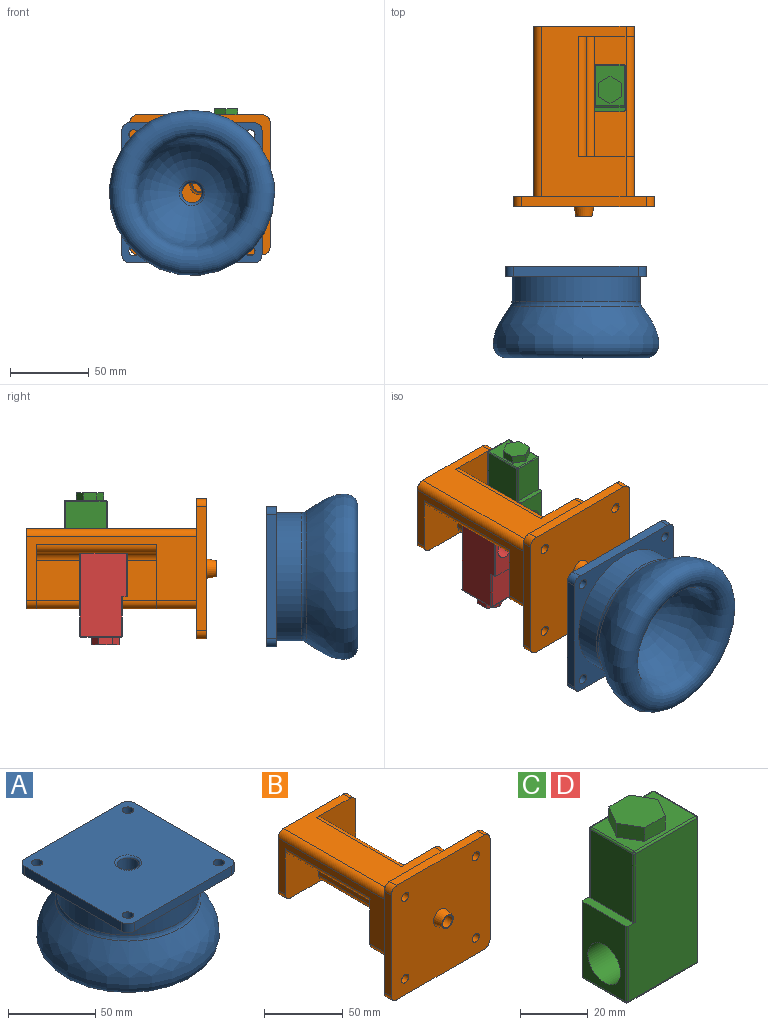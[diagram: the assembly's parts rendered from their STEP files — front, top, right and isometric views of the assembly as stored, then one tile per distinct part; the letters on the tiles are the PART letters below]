
ASSEMBLY  parts=4 mates=5
PART A: 20 faces, bbox 105x105x57.9 mm
  f0: plane 88.9x88.9mm, normal (0,0,-1), area 2565.7mm2, adj f1,f6,f7,f8,f9,f10,f11,f12
  f1: cylinder r=5.08mm len=6.35mm, axis (0,0,-1), area 50.7mm2, adj f0,f2,f6,f12
  f2: plane 88.9x88.9mm, normal (0,0,1), area 7572mm2, adj f1,f3,f6,f7,f8,f9,f10,f11
  f3: torus R=7.62mm, axis (0,0,1), area 85.4mm2, adj f2,f4
  f4: cylinder r=6.35mm len=15.18mm, axis (0,0,1), area 605.8mm2, adj f3,f5
  f5: torus R=9.53mm, axis (0,0,-1), area 151.2mm2, adj f4
  f6: plane 78.74x6.35mm, normal (-1,0,0), area 500mm2, adj f0,f1,f2,f7
  f7: cylinder r=5.08mm len=6.35mm, axis (0,0,1), area 50.7mm2, adj f0,f2,f6,f8
  f8: plane 78.74x6.35mm, normal (0,-1,0), area 500mm2, adj f0,f2,f7,f9
  f9: cylinder r=5.08mm len=6.35mm, axis (0,0,-1), area 50.7mm2, adj f0,f2,f8,f10
  f10: plane 78.74x6.35mm, normal (1,0,0), area 500mm2, adj f0,f2,f9,f11
  f11: cylinder r=5.08mm len=6.35mm, axis (0,0,1), area 50.7mm2, adj f0,f2,f10,f12
  f12: plane 78.74x6.35mm, normal (0,1,0), area 500mm2, adj f0,f1,f2,f11
  f13: cylinder r=3.17mm len=6.35mm, axis (0,0,1), area 126.7mm2, adj f0,f2
  f14: cylinder r=3.17mm len=6.35mm, axis (0,0,1), area 126.7mm2, adj f0,f2
  f15: cylinder r=3.17mm len=6.35mm, axis (0,0,1), area 126.7mm2, adj f0,f2
  f16: cylinder r=3.17mm len=6.35mm, axis (0,0,1), area 126.7mm2, adj f0,f2
  f17: cylinder r=40.64mm len=81.28mm, axis (0,0,1), area 4062mm2, adj f0,f18
  f18: torus R=45.72mm, axis (0,0,1), area 899mm2, adj f17
  f19: revolved ~104.97x104.97mm, area 44213.3mm2
PART B: 50 faces, bbox 88.9x120.7x88.9 mm
  f0: plane 53.34x20.32mm, normal (0,-1,0), area 830.5mm2, adj f14,f15,f16,f17,f18,f19
  f1: plane 40.64x35.24mm, normal (0,-1,0), area 1072.6mm2, adj f2,f3,f10,f11,f42,f43,f44,f46
  f2: plane 107.95x40.64mm, normal (1,0,0), area 1677.4mm2, adj f1,f7,f13,f31,f39,f42,f46,f47
  f3: plane 107.95x53.34mm, normal (0,0,1), area 3459.7mm2, adj f1,f7,f13,f31,f39,f44,f46,f49
  f4: plane 107.95x40.64mm, normal (-1,0,0), area 1677.4mm2, adj f6,f7,f12,f31,f38,f40,f48,f49
  f5: plane 107.95x53.34mm, normal (0,0,-1), area 3459.7mm2, adj f6,f7,f12,f31,f38,f45,f47,f48
  f6: plane 40.64x35.24mm, normal (0,-1,0), area 1072.6mm2, adj f4,f5,f8,f9,f40,f41,f45,f48
  f7: plane 63.5x50.8mm, normal (0,1,0), area 3203.6mm2, adj f2,f3,f4,f5,f46,f47,f48,f49
  f8: plane 76.2x20mm, normal (0,0,-1), area 1524.2mm2, adj f6,f12,f40,f41
  f9: plane 76.2x25.4mm, normal (-1,0,0), area 1935.5mm2, adj f6,f12,f41,f45
  f10: plane 76.2x20mm, normal (0,0,1), area 1524.2mm2, adj f1,f13,f42,f43
  f11: plane 76.2x25.4mm, normal (1,0,0), area 1935.5mm2, adj f1,f13,f43,f44
  f12: plane 40.64x35.24mm, normal (0,1,0), area 945.9mm2, adj f4,f5,f8,f9,f15,f38,f40,f41
  f13: plane 40.64x35.24mm, normal (0,1,0), area 945.9mm2, adj f2,f3,f10,f11,f14,f39,f42,f43
  f14: cylinder r=6.35mm len=12.7mm, axis (0,1,0), area 506.7mm2, adj f0,f13
  f15: cylinder r=6.35mm len=12.7mm, axis (0,1,0), area 506.7mm2, adj f0,f12
  f16: plane 53.34x12.7mm, normal (0,0,1), area 677.4mm2, adj f0,f17,f19,f20
  f17: plane 20.32x12.7mm, normal (1,0,0), area 258.1mm2, adj f0,f16,f18,f20
  f18: plane 53.34x12.7mm, normal (0,0,-1), area 677.4mm2, adj f0,f17,f19,f20
  f19: plane 20.32x12.7mm, normal (-1,0,0), area 258.1mm2, adj f0,f16,f18,f20
  f20: plane 53.34x20.32mm, normal (0,1,0), area 1021.8mm2, adj f16,f17,f18,f19,f29
  f21: plane 78.74x6.35mm, normal (-1,0,0), area 500mm2, adj f30,f31,f34,f37
  f22: plane 78.74x6.35mm, normal (0,0,-1), area 500mm2, adj f30,f31,f34,f35
  f23: plane 78.74x6.35mm, normal (1,0,0), area 500mm2, adj f30,f31,f35,f36
  f24: plane 78.74x6.35mm, normal (0,0,1), area 500mm2, adj f30,f31,f36,f37
  f25: cylinder r=3.17mm len=6.35mm, axis (0,1,0), area 126.7mm2, adj f30,f31
  f26: cylinder r=3.17mm len=6.35mm, axis (0,1,0), area 126.7mm2, adj f30,f31
  f27: cylinder r=3.17mm len=6.35mm, axis (0,1,0), area 126.7mm2, adj f30,f31
  f28: cylinder r=3.17mm len=6.35mm, axis (0,1,0), area 126.7mm2, adj f30,f31
  f29: cylinder r=4.45mm len=12.7mm, axis (0,1,0), area 354.7mm2, adj f20,f32
  f30: plane 88.9x88.9mm, normal (0,-1,0), area 7627.7mm2, adj f21,f22,f23,f24,f25,f26,f27,f28
  f31: plane 88.9x88.9mm, normal (0,1,0), area 4550.7mm2, adj f2,f3,f4,f5,f21,f22,f23,f24
  f32: plane 10.16x10.16mm, normal (0,-1,0), area 19mm2, adj f29,f33
  f33: cone r=5.08mm half-angle=11.3deg, axis (0,1,0), area 232.5mm2, adj f30,f32
  f34: cylinder r=5.08mm len=6.35mm, axis (0,1,0), area 50.7mm2, adj f21,f22,f30,f31
  f35: cylinder r=5.08mm len=6.35mm, axis (0,-1,0), area 50.7mm2, adj f22,f23,f30,f31
  f36: cylinder r=5.08mm len=6.35mm, axis (0,1,0), area 50.7mm2, adj f23,f24,f30,f31
  f37: cylinder r=5.08mm len=6.35mm, axis (0,-1,0), area 50.7mm2, adj f21,f24,f30,f31
  f38: cylinder r=5.08mm len=25.4mm, axis (0,1,0), area 202.7mm2, adj f4,f5,f12,f31
  f39: cylinder r=5.08mm len=25.4mm, axis (0,1,0), area 202.7mm2, adj f2,f3,f13,f31
  f40: cylinder r=5.08mm len=76.2mm, axis (0,1,0), area 608mm2, adj f4,f6,f8,f12
  f41: cylinder r=5.08mm len=76.2mm, axis (0,-1,0), area 608mm2, adj f6,f8,f9,f12
  f42: cylinder r=5.08mm len=76.2mm, axis (0,-1,0), area 608mm2, adj f1,f2,f10,f13
  f43: cylinder r=5.08mm len=76.2mm, axis (0,1,0), area 608mm2, adj f1,f10,f11,f13
  f44: cylinder r=5.08mm len=76.2mm, axis (0,1,0), area 608mm2, adj f1,f3,f11,f13
  f45: cylinder r=5.08mm len=76.2mm, axis (0,1,0), area 608mm2, adj f5,f6,f9,f12
  f46: cylinder r=5.08mm len=6.35mm, axis (0,1,0), area 50.7mm2, adj f1,f2,f3,f7
  f47: cylinder r=5.08mm len=107.95mm, axis (0,-1,0), area 861.4mm2, adj f2,f5,f7,f31
  f48: cylinder r=5.08mm len=6.35mm, axis (0,1,0), area 50.7mm2, adj f4,f5,f6,f7
  f49: cylinder r=5.08mm len=107.95mm, axis (0,-1,0), area 861.4mm2, adj f3,f4,f7,f31
PART C: 42 faces, bbox 30x19.1x58.4 mm
  f0: plane 19.05x3.64mm, normal (0,0,1), area 57.1mm2, adj f1,f4,f5,f8,f9,f10,f24,f27
  f1: plane 27.37x17.78mm, normal (-1,0,0), area 338.8mm2, adj f0,f6,f24,f27,f30
  f2: plane 28.73x17.78mm, normal (0,0,-1), area 485.7mm2, adj f21,f25,f26,f30,f31,f33
  f3: plane 52.13x17.78mm, normal (1,0,0), area 779.1mm2, adj f6,f7,f11,f15,f21
  f4: plane 52.13x28.73mm, normal (0,-1,0), area 1423.4mm2, adj f0,f10,f11,f19,f24,f25
  f5: plane 52.13x28.73mm, normal (0,1,0), area 1423.4mm2, adj f0,f7,f8,f14,f26,f27
  f6: cylinder r=6.86mm len=30mm, axis (1,0,0), area 1292.7mm2, adj f1,f3
  f7: cylinder r=0.64mm len=52.13mm, axis (0,0,-1), area 52mm2, adj f3,f5,f13,f23
  f8: cylinder r=0.64mm len=24.77mm, axis (0,0,-1), area 24.7mm2, adj f0,f5,f9,f16
  f9: plane 24.77x17.78mm, normal (-1,0,0), area 440.3mm2, adj f0,f8,f10,f18
  f10: cylinder r=0.64mm len=24.77mm, axis (0,0,-1), area 24.7mm2, adj f0,f4,f9,f20
  f11: cylinder r=0.64mm len=52.13mm, axis (0,0,-1), area 52mm2, adj f3,f4,f17,f22
  f12: plane 25.73x17.78mm, normal (0,0,1), area 262.6mm2, adj f14,f15,f18,f19,f35,f36,f37,f38
  f13: sphere r=0.64mm, area 0.6mm2, adj f7,f14,f15
  f14: cylinder r=0.64mm len=25.73mm, axis (-1,0,0), area 25.7mm2, adj f5,f12,f13,f16
  f15: cylinder r=0.64mm len=17.78mm, axis (0,1,0), area 17.7mm2, adj f3,f12,f13,f17
  f16: sphere r=0.64mm, area 0.6mm2, adj f8,f14,f18
  f17: sphere r=0.64mm, area 0.6mm2, adj f11,f15,f19
  f18: cylinder r=0.64mm len=17.78mm, axis (0,1,0), area 17.7mm2, adj f9,f12,f16,f20
  f19: cylinder r=0.64mm len=25.73mm, axis (1,0,0), area 25.7mm2, adj f4,f12,f17,f20
  f20: sphere r=0.64mm, area 0.6mm2, adj f10,f18,f19
  f21: cylinder r=0.64mm len=17.78mm, axis (0,-1,0), area 17.7mm2, adj f2,f3,f22,f23
  f22: sphere r=0.64mm, area 0.6mm2, adj f11,f21,f25
  f23: sphere r=0.64mm, area 0.6mm2, adj f7,f21,f26
  f24: cylinder r=0.64mm len=27.37mm, axis (0,0,1), area 27.3mm2, adj f0,f1,f4,f28
  f25: cylinder r=0.64mm len=28.73mm, axis (-1,0,0), area 28.7mm2, adj f2,f4,f22,f28
  f26: cylinder r=0.64mm len=28.73mm, axis (1,0,0), area 28.7mm2, adj f2,f5,f23,f29
  f27: cylinder r=0.64mm len=27.37mm, axis (0,0,-1), area 27.3mm2, adj f0,f1,f5,f29
  f28: sphere r=0.64mm, area 0.6mm2, adj f24,f25,f30
  f29: sphere r=0.64mm, area 0.6mm2, adj f26,f27,f30
  f30: cylinder r=0.64mm len=17.78mm, axis (0,1,0), area 17.7mm2, adj f1,f2,f28,f29
  f31: cylinder r=2mm len=4mm, axis (0,0,-1), area 50.3mm2, adj f2,f32
  f32: plane 4x4mm, normal (0,0,-1), area 12.6mm2, adj f31
  f33: cylinder r=2mm len=4mm, axis (0,0,-1), area 50.3mm2, adj f2,f34
  f34: plane 4x4mm, normal (0,0,-1), area 12.6mm2, adj f33
  f35: plane 7.5x5mm, normal (-0.87,0.5,0), area 43.3mm2, adj f12,f36,f40,f41
  f36: plane 7.5x5mm, normal (-0.87,-0.5,0), area 43.3mm2, adj f12,f35,f37,f41
  f37: plane 8.66x5mm, normal (0,-1,0), area 43.3mm2, adj f12,f36,f38,f41
  f38: plane 7.5x5mm, normal (0.87,-0.5,0), area 43.3mm2, adj f12,f37,f39,f41
  f39: plane 7.5x5mm, normal (0.87,0.5,0), area 43.3mm2, adj f12,f38,f40,f41
  f40: plane 8.66x5mm, normal (0,1,0), area 43.3mm2, adj f12,f35,f39,f41
  f41: plane 17.32x15mm, normal (0,0,1), area 194.9mm2, adj f35,f36,f37,f38,f39,f40
PART D: same geometry as C
PLACE A rot(axis=(-1,0,0),90deg) t=(-100.7,-93.26,-56.96)mm
PLACE B t=(-55.97,89.57,-35.94)mm fixed
PLACE C rot(axis=(0,0,1),90deg) t=(-84.46,50.66,-33.64)mm
PLACE D rot(axis=(-0.71,-0.71,0),180deg) t=(-98.43,40.9,-70.11)mm
MATE slider B.f15 <-> D.f6  axis (0,-1,0) through (-107.96,7.02,-51.88)mm
MATE planar B.f8 <-> D.f2  axis (0,0,-1) through (-108.12,45.12,-41.72)mm
MATE slider A.f13 <-> B.f26  axis (0,1,0) through (-59.7,-62.83,-20.13)mm
MATE planar B.f10 <-> C.f2  axis (0,0,1) through (-74.78,45.12,-62.04)mm
MATE slider C.f6 <-> B.f14  axis (0,1,0) through (-74.94,35.23,-52.04)mm
